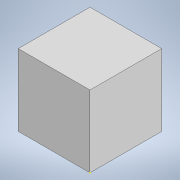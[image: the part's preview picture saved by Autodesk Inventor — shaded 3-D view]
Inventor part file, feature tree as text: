
AUTODESK INVENTOR PART (.ipt)
format: ipt  version: 2021 (Build 250183000, 183)  size: 108,032 bytes
history: native  units: in
note: dims shown in document units (in); Inventor stores cm internally (conversion verified against a paired STEP export)
features: sketch x3, extrude x2
ambient origin geometry x8: Origin, YZ Plane, XZ Plane, XY Plane, X Axis, Y Axis, Z Axis, Center Point
bodies: Solid1 (feature_tree)
feature tree (5):
  sketch  "Sketch1"  dims[d1=0.6299in d2=0.6299in]
  extrude  "Extrusion1"  Depth=0.6299in
  extrude  "Extrusion2"  Depth=0.5118in TaperAngle=0.0deg
  sketch  "Sketch2"  dims[d8=0.6299in d9=0.0in d18=0.5118in d19=0.0in]
  sketch  "Sketch3"  dims[d22=0.5118in d23=0.1417in d25=0.0709in d26=0.5118in d27=0.1417in]
